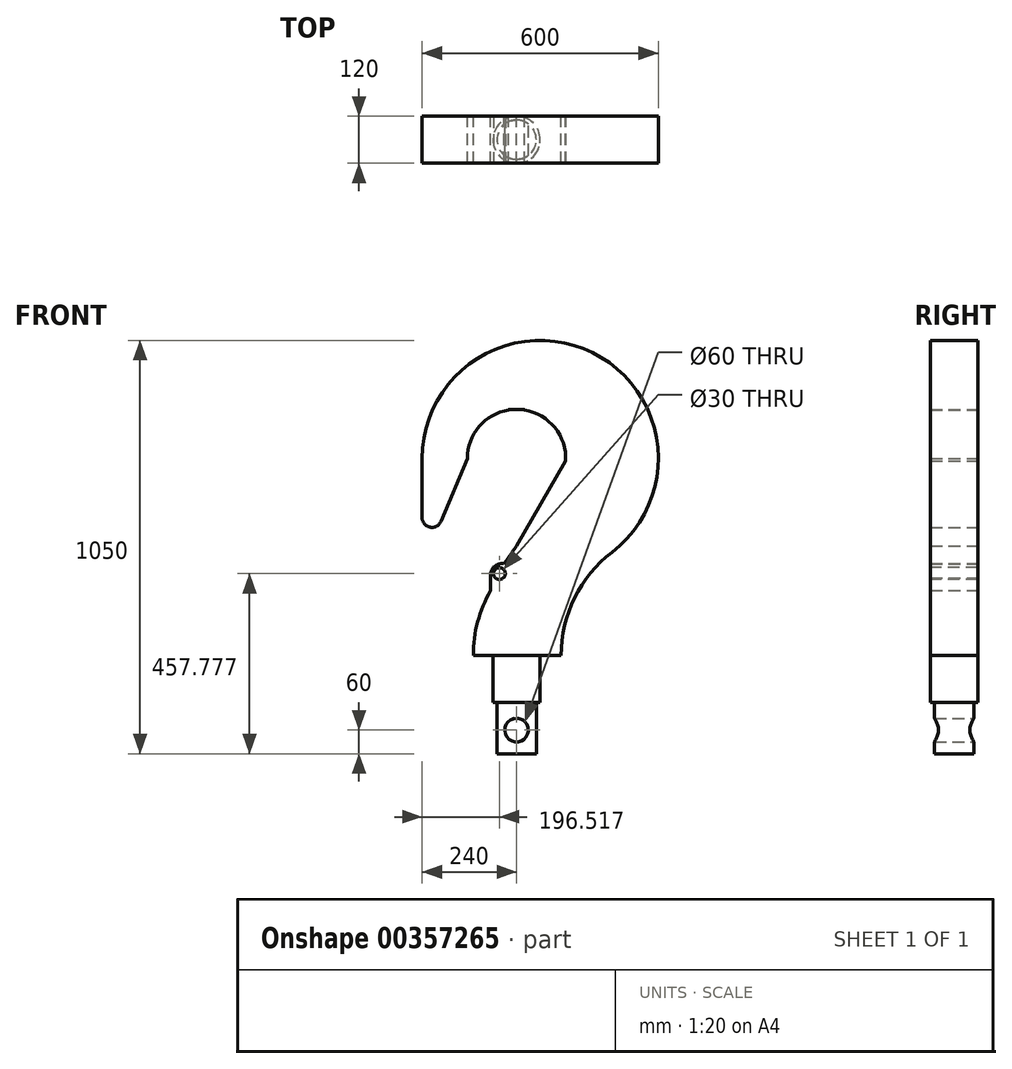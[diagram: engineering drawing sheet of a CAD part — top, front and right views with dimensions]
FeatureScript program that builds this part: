
annotation { "Feature Type Name" : "Feature", "Feature Type Description" : "" }
export const myFeature = defineFeature(function(context is Context, id is Id, definition is map)
    precondition{}
    {
        {
            var Q0;
            Q0=qCreatedBy(makeId("Front.planeOp"),FACE);
            var sketch = newSketch(context, id + "F0", { "sketchPlane" : qUnion([Q0])});
            skArc(sketch, "E0", {"start": v(242.51, 261.9) * mm, "mid": v(147.34, 146.03) * mm, "end": v(113.28, 0) * mm});
            skArc(sketch, "E1", {"start": v(-66.06, 164.53) * mm, "mid": v(-98.83, 85.15) * mm, "end": v(-110, 0) * mm});
            skLineSegment(sketch, "E2", {"start": v(0, 898.51) * mm, "end": v(0, -968.16) * mm, "construction": true});
            skArc(sketch, "E3", {"start": v(124.84, 493.61) * mm, "mid": v(97.24, 578.55) * mm, "end": v(20, 623.39) * mm});
            skArc(sketch, "E4", {"start": v(242.51, 261.9) * mm, "mid": v(192.75, 769.03) * mm, "end": v(-240, 500) * mm});
            skLineSegment(sketch, "E5", {"start": v(124.84, 493.61) * mm, "end": v(0, 278.41) * mm});
            skLineSegment(sketch, "E6", {"start": v(-607.5, 0) * mm, "end": v(1252.05, 0) * mm, "construction": true});
            skLineSegment(sketch, "E7", {"start": v(0, 500) * mm, "end": v(-349.97, 500) * mm, "construction": true});
            skLineSegment(sketch, "E8", {"start": v(-240, 500) * mm, "end": v(-125, 500) * mm});
            skArc(sketch, "E9", {"start": v(-240, 350) * mm, "mid": v(-219.93, 325.5) * mm, "end": v(-191.94, 340.33) * mm});
            skLineSegment(sketch, "E10", {"start": v(-240, 500) * mm, "end": v(-240, 350) * mm});
            skLineSegment(sketch, "E11", {"start": v(-125, 500) * mm, "end": v(-191.94, 340.33) * mm});
            skLineSegment(sketch, "E12", {"start": v(-110, 0) * mm, "end": v(113.28, 0) * mm});
            skPoint(sketch, "E13.oppositeSnap0", {"position": v(20, 623.39) * mm});
            skLineSegment(sketch, "E13.top", {"start": v(-20, 624.95) * mm, "end": v(20, 624.95) * mm});
            skLineSegment(sketch, "E13.left", {"start": v(-20, 623.39) * mm, "end": v(-20, 624.95) * mm});
            skLineSegment(sketch, "E13.right", {"start": v(20, 623.39) * mm, "end": v(20, 624.95) * mm});
            skArc(sketch, "E14.trimOffspring", {"start": v(-20, 623.39) * mm, "mid": v(-95.2, 581) * mm, "end": v(-125, 500) * mm});
            skLineSegment(sketch, "E15.trimOffspring", {"start": v(55.5, 612) * mm, "end": v(68.67, 612) * mm, "construction": true});
            skLineSegment(sketch, "E16", {"start": v(-66.06, 164.53) * mm, "end": v(-66.06, 197.07) * mm});
            skArc(sketch, "E17", {"start": v(-31.67, 232.57) * mm, "mid": v(-58.2, 223.86) * mm, "end": v(-66.06, 197.07) * mm});
            skLineSegment(sketch, "E18", {"start": v(-31.67, 232.57) * mm, "end": v(0, 278.41) * mm});
            skSolve(sketch);
        }
        {
            var Q0;
            Q0=qCreatedBy(makeId("Front.planeOp"),FACE);
            var sketch = newSketch(context, id + "F1", { "sketchPlane" : qUnion([Q0])});
            skLineSegment(sketch, "E19", {"start": v(-50, -250) * mm, "end": v(0, -250) * mm});
            skLineSegment(sketch, "E20", {"start": v(-60, 0) * mm, "end": v(0, 0) * mm});
            skLineSegment(sketch, "E21", {"start": v(0, 0) * mm, "end": v(0, -250) * mm});
            skLineSegment(sketch, "E22", {"start": v(-60, -120) * mm, "end": v(-60, 0) * mm});
            skLineSegment(sketch, "E23", {"start": v(-60, -120) * mm, "end": v(-50, -120) * mm});
            skLineSegment(sketch, "E24", {"start": v(-50, -120) * mm, "end": v(-50, -250) * mm});
            skSolve(sketch);
        }
        {
            var Q0;
            Q0=qSketchRegion(id+"F1",true);
            var Q1;
            Q1=sQuery(id+"F1.wireOp",EDGE,"E21");
            revolve(context, id + "F2", {"entities" : qUnion([Q0]), "axis" : qUnion([Q1]), "revolveType" : RevolveType.FULL});
        }
        {
            var Q0;
            Q0=makeQuery(id+"F0.imprint","IMPRINT",FACE,{"disambiguationData":[TD([[makeQuery(id+"F0.imprint","IMPRINT",EDGE,{"derivedFrom":sQuery(id+"F0.wireOp",EDGE,"E0")}),-1.0]])]});
            var Q1;
            Q1=makeQuery(id+"F0.imprint","IMPRINT",FACE,{"disambiguationData":[TD([[makeQuery(id+"F0.imprint","IMPRINT",EDGE,{"derivedFrom":sQuery(id+"F0.wireOp",EDGE,"E8")}),-1.0]])]});
            extrude(context, id + "F3", {"entities" : qUnion([Q0, Q1]), "operationType" : NewBodyOperationType.ADD, "endBound" : BoundingType.SYMMETRIC, "depth" : 120 * mm});
        }
        {
            var Q0;
            Q0=qCreatedBy(makeId("Front.planeOp"),FACE);
            var sketch = newSketch(context, id + "F4", { "sketchPlane" : qUnion([Q0])});
            skCircle(sketch, "E25", {"center": v(0, -190) * mm, "radius": 30 * mm});
            skSolve(sketch);
        }
        {
            var Q0;
            Q0=qSketchRegion(id+"F4",true);
            extrude(context, id + "F5", {"entities" : qUnion([Q0]), "operationType" : NewBodyOperationType.REMOVE, "endBound" : BoundingType.SYMMETRIC, "depth" : 224 * mm});
        }
        {
            var Q0;
            Q0=makeQuery(id+"F3.opExtrude","CAP_FACE",FACE,{"disambiguationData":[OSD([sQuery(id+"F0.wireOp",EDGE,"E0"),sQuery(id+"F0.wireOp",EDGE,"E1"),sQuery(id+"F0.wireOp",EDGE,"E3"),sQuery(id+"F0.wireOp",EDGE,"E4"),sQuery(id+"F0.wireOp",EDGE,"E5"),sQuery(id+"F0.wireOp",EDGE,"E9"),sQuery(id+"F0.wireOp",EDGE,"E10"),sQuery(id+"F0.wireOp",EDGE,"E11"),sQuery(id+"F0.wireOp",EDGE,"E12"),sQuery(id+"F0.wireOp",EDGE,"E13.top"),sQuery(id+"F0.wireOp",EDGE,"E13.left"),sQuery(id+"F0.wireOp",EDGE,"E13.right"),sQuery(id+"F0.wireOp",EDGE,"E14.trimOffspring")])],"isStart":false});
            var sketch = newSketch(context, id + "F6", { "sketchPlane" : qUnion([Q0])});
            skCircle(sketch, "E26", {"center": v(-43.48, 207.78) * mm, "radius": 15 * mm});
            skSolve(sketch);
        }
        {
            var Q0;
            Q0=qSketchRegion(id+"F6",true);
            var Q1;
            Q1=makeQuery(id+"F6.imprint","IMPRINT",FACE,{"disambiguationData":[TD([[makeQuery(id+"F6.imprint","IMPRINT",EDGE,{"derivedFrom":sQuery(id+"F6.wireOp",EDGE,"E26")}),1.0]])]});
            extrude(context, id + "F7", {"entities" : qUnion([Q0, Q1]), "operationType" : NewBodyOperationType.REMOVE, "endBound" : BoundingType.SYMMETRIC, "oppositeDirection" : true, "depth" : 326 * mm});
        }
    });
